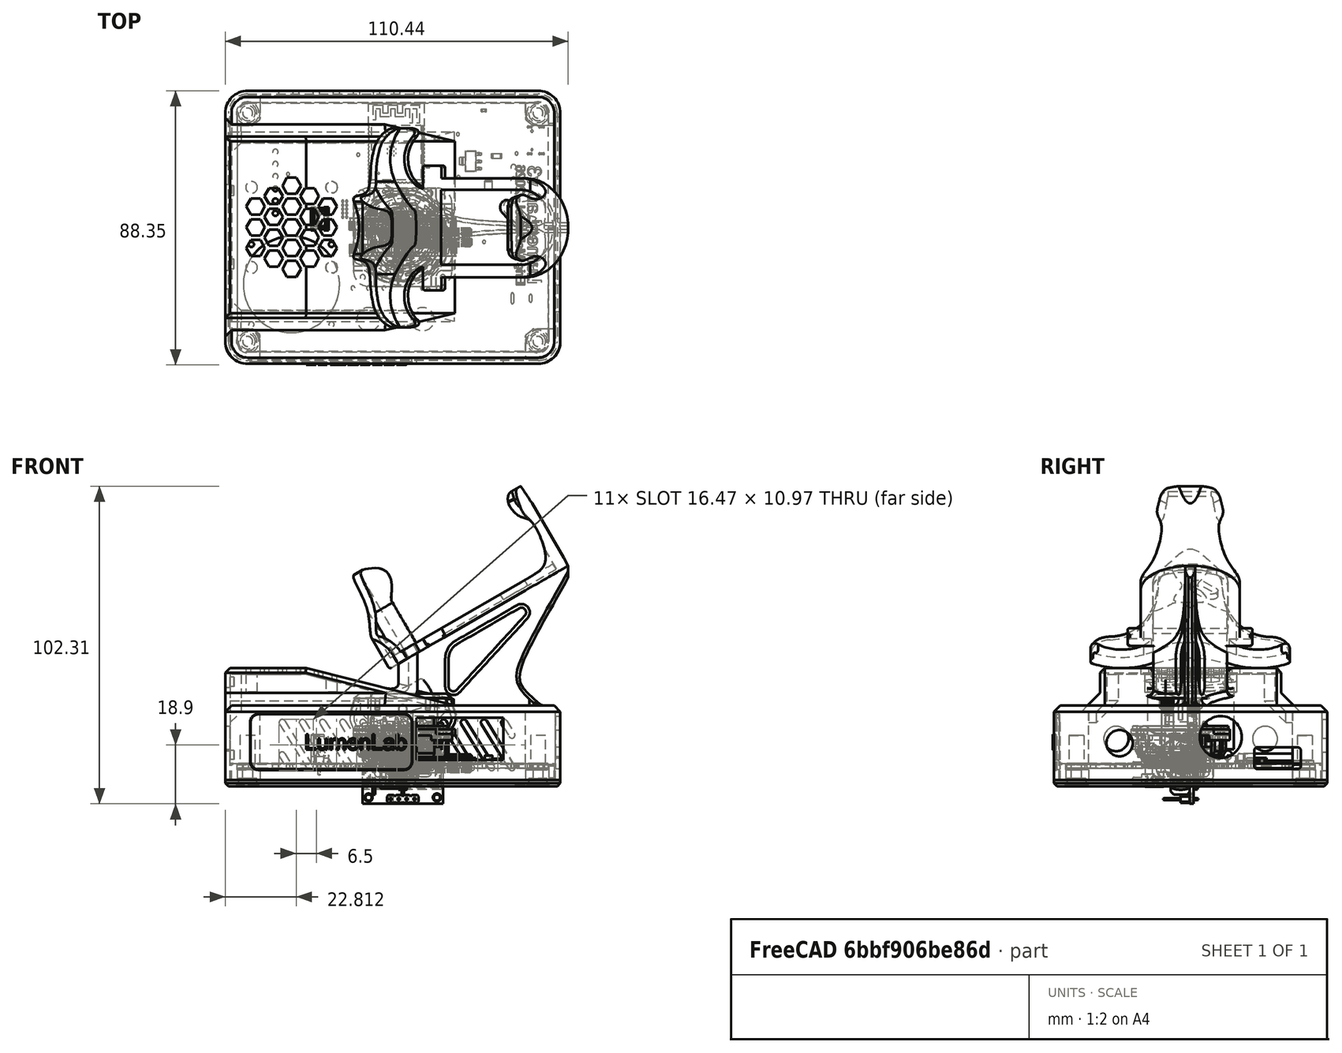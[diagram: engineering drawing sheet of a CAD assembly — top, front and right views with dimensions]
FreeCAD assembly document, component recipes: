
FREECAD ASSEMBLY — COMPONENT RECIPES ("lumenlab-platform-enclosure")

This assembly document has 22 components, labeled P0..P21 below (a component is one placed body or linked part). 21 of them carry a construction recipe — the FreeCAD feature program that regenerates the part from scratch, quoted from this document or its linked companion documents; the rest are supplied as boundary geometry only. No exploded tour is included for this assembly.
NOTE — document 2 of 2 of this assembly tour. The two overview renders and the header above are repeated from document 1; the component sections below continue where the previous document stopped.
COMPONENT P17 — recipe-attached ("saddle", modeled in this document).
Construction recipe (the document's own serialized feature program — sketch geometry with constraints, then the solid features built on it; lengths are millimeters unless a unit is written):

FEATURE [PartDesign::SubShapeBinder] Binder006
  BindCopyOnChange = 0
  BindMode = 0
  ClaimChildren = false
  Context = -> Body016 [Binder006.]
  Fuse = false
  MakeFace = true
  OffsetFill = false
  OffsetIntersection = false
  OffsetJoinType = 0
  OffsetOpenResult = false
  PartialLoad = false
  Refine = true
  Relative = true
  Support = -> [Body001]
  _Version = 2
FEATURE [PartDesign::SubShapeBinder] Binder007
  BindCopyOnChange = 0
  BindMode = 0
  ClaimChildren = false
  Context = -> Body016 [Binder007.]
  Fuse = false
  MakeFace = true
  OffsetFill = false
  OffsetIntersection = false
  OffsetJoinType = 0
  OffsetOpenResult = false
  PartialLoad = false
  Refine = true
  Relative = true
  Support = -> [PS3_Controller]
  _Version = 2
FEATURE [Sketcher::SketchObject] Sketch050
  ArcFitTolerance = 1e-06
  AttachmentSupport = -> [Binder007]
  ExternalGeometry = -> [Binder007]
  ExternalTypes = [0,0,0,0,0,0,0]
  FullyConstrained = false
  MakeInternals = false
  MapMode = 5
  Placement = pos=(-15.7431,5e-16,27.2678) rot=(0.965926,0,0.258819;3.14159rad)
  _ExternalGeoVersion = 1
  sketch-geometry (44):
    g0: LineSegment StartX=14.7182 StartY=28.9768 StartZ=0 EndX=18.1182 EndY=28.9768 EndZ=0
    g1: LineSegment StartX=14.7182 StartY=-35.1235 StartZ=0 EndX=18.1182 EndY=-35.1235 EndZ=0
    g2: ArcOfCircle CenterX=28.7277 CenterY=18.953 CenterZ=0 NormalX=0 NormalY=0 NormalZ=1 AngleXU=0 Radius=17.2262 StartAngle=2.52054 EndAngle=3.77326
    g3: ArcOfCircle CenterX=28.7277 CenterY=-25.0997 CenterZ=0 NormalX=0 NormalY=0 NormalZ=1 AngleXU=0 Radius=17.2262 StartAngle=2.50993 EndAngle=3.76265
    g4: ArcOfCircle CenterX=28.7277 CenterY=18.953 CenterZ=0 NormalX=0 NormalY=0 NormalZ=1 AngleXU=0 Radius=10 StartAngle=2.27093 EndAngle=4.40385
    g5: ArcOfCircle CenterX=28.7277 CenterY=-25.0997 CenterZ=0 NormalX=0 NormalY=0 NormalZ=1 AngleXU=0 Radius=10 StartAngle=1.87933 EndAngle=3.98193
    g6: LineSegment StartX=25.6911 StartY=9.42521 StartZ=0 EndX=25.6911 EndY=16.3262 EndZ=0
    g7: LineSegment StartX=25.6911 StartY=-15.5719 StartZ=0 EndX=25.6911 EndY=-22.3413 EndZ=0
    g8: LineSegment StartX=32.5059 StartY=12.8763 StartZ=0 EndX=62.0059 EndY=12.8763 EndZ=0
    g9: ArcOfCircle CenterX=62.0059 CenterY=-3.07369 CenterZ=0 NormalX=0 NormalY=0 NormalZ=1 AngleXU=0 Radius=15.95 StartAngle=4.71239 EndAngle=7.85398
    g10: Circle [constr] CenterX=18.1182 CenterY=28.9768 CenterZ=0 NormalX=0 NormalY=0 NormalZ=1 AngleXU=0 Radius=1
    g11: Circle [constr] CenterX=24.3003 CenterY=29.1669 CenterZ=0 NormalX=0 NormalY=0 NormalZ=1 AngleXU=0 Radius=1
    g12: Circle [constr] CenterX=22.2845 CenterY=26.6006 CenterZ=0 NormalX=0 NormalY=0 NormalZ=1 AngleXU=0 Radius=1
    g13: BSplineCurve PolesCount=3 KnotsCount=2 Degree=2 IsPeriodic=0
    g14: GeomPoint [constr] X=18.1182 Y=28.9768 Z=0
    g15: GeomPoint [constr] X=22.2845 Y=26.6006 Z=0
    g16: Circle [constr] CenterX=18.1182 CenterY=-35.1235 CenterZ=0 NormalX=0 NormalY=0 NormalZ=1 AngleXU=0 Radius=1
    g17: Circle [constr] CenterX=24.3003 CenterY=-35.3594 CenterZ=0 NormalX=0 NormalY=0 NormalZ=1 AngleXU=0 Radius=1
    g18: Circle [constr] CenterX=22.0556 CenterY=-32.5484 CenterZ=0 NormalX=0 NormalY=0 NormalZ=1 AngleXU=0 Radius=1
    g19: BSplineCurve PolesCount=3 KnotsCount=2 Degree=2 IsPeriodic=0
    g20: GeomPoint [constr] X=18.1182 Y=-35.1235 Z=0
    g21: GeomPoint [constr] X=22.0556 Y=-32.5484 Z=0
    g22: Circle [constr] CenterX=14.8254 CenterY=8.78113 CenterZ=0 NormalX=0 NormalY=0 NormalZ=1 AngleXU=0 Radius=1
    g23: Circle [constr] CenterX=22.5059 CenterY=-3.07336 CenterZ=0 NormalX=0 NormalY=0 NormalZ=1 AngleXU=0 Radius=1
    g24: Circle [constr] CenterX=14.8254 CenterY=-14.9279 CenterZ=0 NormalX=0 NormalY=0 NormalZ=1 AngleXU=0 Radius=1
    g25: BSplineCurve PolesCount=3 KnotsCount=2 Degree=2 IsPeriodic=0
    g26: GeomPoint [constr] X=14.8254 Y=8.78113 Z=0
    g27: GeomPoint [constr] X=14.8254 Y=-14.9279 Z=0
    g28: LineSegment [constr] StartX=29.7892 StartY=4.11327 StartZ=0 EndX=22.5059 EndY=-3.07336 EndZ=0
    g29: LineSegment [constr] StartX=29.7892 StartY=-10.26 StartZ=0 EndX=22.5059 EndY=-3.07336 EndZ=0
    g30: LineSegment StartX=32.5059 StartY=12.8763 StartZ=0 EndX=32.5059 EndY=16.3262 EndZ=0
    g31: LineSegment StartX=31.7836 StartY=17.0486 StartZ=0 EndX=26.4134 EndY=17.0486 EndZ=0
    g32: LineSegment StartX=62.0059 StartY=-19.0237 StartZ=0 EndX=32.5059 EndY=-19.0237 EndZ=0
    g33: LineSegment StartX=32.5059 StartY=-19.0237 StartZ=0 EndX=32.5059 EndY=-22.3413 EndZ=0
    g34: LineSegment StartX=31.7836 StartY=-23.0637 StartZ=0 EndX=26.4134 EndY=-23.0637 EndZ=0
    g35: ArcOfCircle CenterX=31.7836 CenterY=16.3262 CenterZ=0 NormalX=0 NormalY=0 NormalZ=1 AngleXU=0 Radius=0.722378 StartAngle=2.3e-15 EndAngle=1.5708
    g36: GeomPoint [constr] X=32.5059 Y=17.0486 Z=0
    g37: ArcOfCircle CenterX=26.4134 CenterY=16.3262 CenterZ=0 NormalX=0 NormalY=0 NormalZ=1 AngleXU=0 Radius=0.722378 StartAngle=1.5708 EndAngle=3.14159
    g38: GeomPoint [constr] X=25.6911 Y=17.0486 Z=0
    g39: ArcOfCircle CenterX=31.7836 CenterY=-22.3413 CenterZ=0 NormalX=0 NormalY=0 NormalZ=1 AngleXU=0 Radius=0.722378 StartAngle=4.71239 EndAngle=6.28319
    g40: GeomPoint [constr] X=32.5059 Y=-23.0637 Z=0
    g41: ArcOfCircle CenterX=26.4134 CenterY=-22.3413 CenterZ=0 NormalX=0 NormalY=0 NormalZ=1 AngleXU=0 Radius=0.722378 StartAngle=3.14159 EndAngle=4.71239
    g42: GeomPoint [constr] X=25.6911 Y=-23.0637 Z=0
    g43: LineSegment [constr] StartX=32.5059 StartY=12.8763 StartZ=0 EndX=32.5059 EndY=-19.0237 EndZ=0
  constraints (91):
    c: Horizontal(g0,g-3)
    c: Horizontal(g1,g-4)
    c: Coincident(g0,g-3)
    c: DistanceX(g0,g0) = 3.4
    c: Coincident(g1,g-4)
    c: DistanceX(g1,g1) = 3.4
    c: Coincident(g2,g-3)
    c: Coincident(g2,g0)
    c: Coincident(g3,g-4)
    c: Coincident(g3,g1)
    c: Coincident(g4,g2)
    c: Coincident(g5,g3)
    c: Radius(g4) = 10
    c: Radius(g5) = 10
    c: Vertical(g4,g5)
    c: Coincident(g6,g4)
    c: Vertical(g6)
    c: Coincident(g7,g5)
    c: Vertical(g7)
    c: Horizontal(g8)
    c: Tangent(g8,g9) = 1.5708
    c: Weight(g10) = 1
    c: Equal(g10,g11)
    c: Equal(g10,g12)
    c: InternalAlignment(g10,g13)
    c: InternalAlignment(g11,g13)
    c: InternalAlignment(g12,g13)
    c: InternalAlignment(g14,g13)
    c: InternalAlignment(g15,g13)
    c: Coincident(g10,g0)
    c: Coincident(g12,g4)
    c: Weight(g16) = 1
    c: Equal(g16,g17)
    c: Equal(g16,g18)
    c: InternalAlignment(g16,g19)
    c: InternalAlignment(g17,g19)
    c: InternalAlignment(g18,g19)
    c: InternalAlignment(g20,g19)
    c: InternalAlignment(g21,g19)
    c: Coincident(g16,g1)
    c: Coincident(g18,g5)
    c: Vertical(g11,g17)
    c: Weight(g22) = 1
    c: Equal(g22,g23)
    c: Equal(g22,g24)
    c: InternalAlignment(g22,g25)
    c: InternalAlignment(g23,g25)
    c: InternalAlignment(g24,g25)
    c: InternalAlignment(g26,g25)
    c: InternalAlignment(g27,g25)
    c: Vertical(g25,g25)
    c: Coincident(g28,g-8)
    c: Coincident(g28,g23)
    c: Coincident(g29,g-8)
    c: Coincident(g29,g23)
    c: Equal(g28,g29)
    c: Coincident(g25,g2)
    c: Coincident(g25,g3)
    c: DistanceX(g8,g8) = 29.5
    c: Coincident(g30,g8)
    c: Vertical(g30)
    c: Horizontal(g31)
    c: Horizontal(g32)
    c: Coincident(g33,g32)
    c: Vertical(g33)
    c: Horizontal(g34)
    c: PointOnObject(g36,g30)
    c: PointOnObject(g36,g31)
    c: Tangent(g30,g35) = -1.5708
    c: Tangent(g31,g35) = -1.5708
    c: PointOnObject(g38,g6)
    c: PointOnObject(g38,g31)
    c: Tangent(g6,g37) = 1.5708
    c: Tangent(g31,g37) = -1.5708
    c: PointOnObject(g40,g33)
    c: PointOnObject(g40,g34)
    c: Tangent(g33,g39) = 1.5708
    c: Tangent(g34,g39) = 1.5708
    c: PointOnObject(g42,g7)
    c: PointOnObject(g42,g34)
    c: Tangent(g7,g41) = -1.5708
    c: Tangent(g34,g41) = 1.5708
    c: Equal(g35,g37)
    c: Equal(g35,g39)
    c: Equal(g35,g41)
    c: DistanceX(g23,g9) = 39.5
    c: Tangent(g32,g9) = 1.5708
    c: Distance(g32,g8) = 31.9
    c: Coincident(g43,g8)
    c: Coincident(g43,g32)
    c: Vertical(g43)
FEATURE [PartDesign::Pad] Pad023
  Direction = (0.5,0,-0.866025)
  Length = 3
  Length2 = 10
  Profile = -> Sketch050
  ReferenceAxis = -> Sketch050 [N_Axis]
  Refine = true
  SideType = 0
  Suppressed = false
  Type = 0
  Type2 = 0
FEATURE [Sketcher::SketchObject] Sketch051
  ArcFitTolerance = 1e-06
  AttachmentSupport = -> [Pad023]
  ExternalGeometry = -> [Binder007,Pad023]
  ExternalTypes = [0,0,0,0,0,0,0,0]
  FullyConstrained = false
  MakeInternals = false
  MapMode = 5
  Placement = pos=(-15.7431,0,27.2678) rot=(0,-1,0;0.523599rad)
  _ExternalGeoVersion = 1
  sketch-geometry (24):
    g0: ArcOfCircle CenterX=28.7277 CenterY=25.0997 CenterZ=0 NormalX=0 NormalY=0 NormalZ=1 AngleXU=0 Radius=15.1872 StartAngle=2.42075 EndAngle=3.62843
    g1: LineSegment [constr] StartX=15.3049 StartY=17.9946 StartZ=0 EndX=15.3049 EndY=-11.8479 EndZ=0
    g2: LineSegment StartX=17.3182 StartY=35.1235 StartZ=0 EndX=14.7182 EndY=35.1235 EndZ=0
    g3-g9: Circle [constr] x7 (B-spline internal-alignment scaffolding for g10; pole/knot coordinates omitted)
    g10: BSplineCurve PolesCount=7 KnotsCount=5 Degree=3 IsPeriodic=0
    g11-g15: GeomPoint [constr] x5 (B-spline internal-alignment scaffolding for g10; pole/knot coordinates omitted)
    g16: LineSegment [constr] StartX=21.176 StartY=8.55829 StartZ=0 EndX=21.176 EndY=-2.41156 EndZ=0
    g17: LineSegment [constr] StartX=23.1344 StartY=12.0134 StartZ=0 EndX=23.1344 EndY=-10.8872 EndZ=0
    g18: ArcOfCircle CenterX=28.7277 CenterY=-18.953 CenterZ=0 NormalX=0 NormalY=0 NormalZ=1 AngleXU=0 Radius=15.1872 StartAngle=2.65476 EndAngle=3.86243
    g19: LineSegment StartX=14.7182 StartY=-28.9768 StartZ=0 EndX=17.3182 EndY=-28.9768 EndZ=0
    g20: LineSegment [constr] StartX=23.1344 StartY=10.26 StartZ=0 EndX=29.7892 EndY=10.26 EndZ=0
    g21: LineSegment [constr] StartX=23.1344 StartY=-4.11327 StartZ=0 EndX=29.7892 EndY=-4.11327 EndZ=0
    g22: LineSegment [constr] StartX=21.176 StartY=8.55829 StartZ=0 EndX=29.7892 EndY=10.26 EndZ=0
    g23: LineSegment [constr] StartX=21.176 StartY=-2.41156 StartZ=0 EndX=29.7892 EndY=-4.11327 EndZ=0
  constraints (42):
    c: Distance(g-3) = 69.7881
    c: Distance(g-3) = 69.7881
    c: PointOnObject(g0,g-6)
    c: DistanceX(g0,g-6) = 0.8
    c: Vertical(g1)
    c: Coincident(g2,g0)
    c: Coincident(g2,g-6)
    c: Coincident(g0,g1)
    c: Weight(g3) = 1
    c: Equal(g3,g4)
    c: Equal(g3,g5)
    c: Equal(g3,g6)
    c: Equal(g3,g8)
    c: Equal(g3,g9)
    c: InternalAlignment(g3-g9 -> g10) x7
    c: InternalAlignment(g11-g15 -> g10) x5
    c: Coincident(g9,g1)
    c: Coincident(g10,g0)
    c: Coincident(g16,g4)
    c: Vertical(g16)
    c: Coincident(g16,g8)
    c: PointOnObject(g5,g17)
    c: PointOnObject(g6,g17)
    c: Coincident(g18,g-19)
    c: Coincident(g18,g10)
    c: Horizontal(g-17,g18)
    c: DistanceX(g18,g-17) = 0.8
    c: Vertical(g17)
    c: Coincident(g19,g-19)
    c: Coincident(g19,g18)
    c: Coincident(g20,g5)
    c: Coincident(g20,g-4)
    c: Horizontal(g20)
    c: Coincident(g21,g7)
    c: Coincident(g21,g-4)
    c: Symmetric(g7,g5,g6)
    c: Coincident(g22,g4)
    c: Coincident(g22,g20)
    c: Coincident(g23,g8)
    c: Coincident(g23,g21)
    c: Equal(g23,g22)
    c: Symmetric(g7,g5,g13)
FEATURE [Sketcher::SketchObject] Sketch054
  ArcFitTolerance = 1e-06
  AttachmentOffset = pos=(0,0,5) rot=(0,0,1;0rad)
  ExternalTypes = [0,0,0]
  FullyConstrained = false
  MakeInternals = false
  MapMode = 5
  Placement = pos=(30.1283,5e-14,17.3946) rot=(0.447214,0.447214,0.774597;1.82348rad)
  _ExternalGeoVersion = 1
  sketch-geometry (24):
    g0: BSplineCurve PolesCount=4 KnotsCount=2 Degree=3 IsPeriodic=0
    g1: ArcOfCircle CenterX=-21.3632 CenterY=31.5542 CenterZ=0 NormalX=0 NormalY=0 NormalZ=1 AngleXU=0 Radius=7.61389 StartAngle=1.74061 EndAngle=3.15052
    g2: LineSegment [constr] StartX=-5.38635 StartY=60.4862 StartZ=0 EndX=-5.38635 EndY=32.2414 EndZ=0
    g3: LineSegment [constr] StartX=-5.38635 StartY=32.2414 StartZ=0 EndX=3.07336 EndY=32.2414 EndZ=0
    g4: LineSegment [constr] StartX=3.07336 StartY=32.2414 StartZ=0 EndX=3.07336 EndY=60.4862 EndZ=0
    g5: LineSegment [constr] StartX=3.07336 StartY=60.4862 StartZ=0 EndX=-5.38635 EndY=60.4862 EndZ=0
    g6: LineSegment [constr] StartX=11.5331 StartY=60.4862 StartZ=0 EndX=3.07336 EndY=60.4862 EndZ=0
    g7: LineSegment [constr] StartX=3.07336 StartY=60.4862 StartZ=0 EndX=3.07336 EndY=32.2414 EndZ=0
    g8: LineSegment [constr] StartX=3.07336 StartY=32.2414 StartZ=0 EndX=11.5331 EndY=32.2414 EndZ=0
    g9: LineSegment [constr] StartX=11.5331 StartY=32.2414 StartZ=0 EndX=11.5331 EndY=60.4862 EndZ=0
    g10: LineSegment [constr] StartX=11.5331 StartY=60.4862 StartZ=0 EndX=-5.38635 EndY=32.2414 EndZ=0
    g11: LineSegment [constr] StartX=-5.38635 StartY=60.4862 StartZ=0 EndX=11.5331 EndY=32.2414 EndZ=0
    g12: GeomPoint [constr] X=3.07336 Y=46.3638 Z=0
    g13: LineSegment [constr] StartX=-28.9768 StartY=60.4862 StartZ=0 EndX=-5.38635 EndY=60.4862 EndZ=0
    g14: LineSegment [constr] StartX=11.5331 StartY=60.4862 StartZ=0 EndX=35.1235 EndY=60.4862 EndZ=0
    g15: ArcOfCircle CenterX=27.5795 CenterY=31.4875 CenterZ=0 NormalX=0 NormalY=0 NormalZ=1 AngleXU=0 Radius=7.54399 StartAngle=6.283 EndAngle=7.68194
    g16: BSplineCurve PolesCount=4 KnotsCount=2 Degree=3 IsPeriodic=0
    g17: LineSegment StartX=-28.9768 StartY=31.4862 StartZ=0 EndX=-28.9768 EndY=31.4861 EndZ=0
    g18: LineSegment StartX=-28.9768 StartY=31.4861 StartZ=0 EndX=-33.2243 EndY=31.4861 EndZ=0
    g19: LineSegment StartX=-33.2243 StartY=31.4861 StartZ=0 EndX=-33.2243 EndY=61.0561 EndZ=0
    g20: LineSegment StartX=39.371 StartY=31.4861 StartZ=0 EndX=39.371 EndY=61.0561 EndZ=0
    g21: LineSegment StartX=35.1235 StartY=31.4861 StartZ=0 EndX=39.371 EndY=31.4861 EndZ=0
    g22: LineSegment StartX=-5.38635 StartY=60.4862 StartZ=0 EndX=11.5331 EndY=60.4862 EndZ=0
    g23: LineSegment StartX=-33.2243 StartY=61.0561 StartZ=0 EndX=39.371 EndY=61.0561 EndZ=0
  constraints (47):
    c: Coincident(g1,g-3) = -1.5708
    c: Tangent(g0,g1) = -1.5708
    c: Coincident(g2,g3)
    c: Coincident(g3,g4)
    c: Coincident(g4,g5)
    c: Coincident(g5,g2)
    c: Vertical(g2)
    c: Vertical(g4)
    c: Horizontal(g3)
    c: Horizontal(g5)
    c: Coincident(g2,g0)
    c: Coincident(g6,g7)
    c: Coincident(g7,g8)
    c: Coincident(g8,g9)
    c: Coincident(g9,g6)
    c: Horizontal(g6)
    c: Horizontal(g8)
    c: Vertical(g7)
    c: Vertical(g9)
    c: Coincident(g7,g3)
    c: Coincident(g10,g6)
    c: Coincident(g10,g2)
    c: Coincident(g11,g2)
    c: Coincident(g11,g8)
    c: Symmetric(g10,g10,g12)
    c: PointOnObject(g12,g4)
    c: Coincident(g13,g-3)
    c: Coincident(g13,g2)
    c: Horizontal(g13)
    c: Coincident(g14,g6)
    c: Coincident(g14,g-4)
    c: Equal(g14,g13)
    c: Tangent(g16,g15) = 1.5708
    c: Tangent(g1,g17) = -1.5708
    c: Coincident(g17,g18)
    c: Coincident(g18,g19)
    c: Vertical(g19)
    c: Horizontal(g18)
    c: DistanceY(g19,g19) = 29.57
    c: Symmetric(g16,g22,g4)
    c: Symmetric(g18,g21,g4)
    c: Symmetric(g18,g21,g4)
    c: Symmetric(g19,g20,g4)
    c: Symmetric(g19,g20,g4)
    c: Coincident(g23,g19)
    c: Coincident(g23,g20)
    c: Coincident(g21,g15)
FEATURE [PartDesign::Plane] DatumPlane003
  AttachmentOffset = pos=(0,0,-1) rot=(0,0,1;0rad)
  AttachmentSupport = -> [Binder006]
  Length = 92.4589
  MapMode = 5
  Placement = pos=(0,0,17.6498) rot=(0,0,1;0rad)
  ResizeMode = 0
  Width = 78.2686
FEATURE [PartDesign::Plane] DatumPlane004
  AttachmentOffset = pos=(0,0,-1) rot=(0,0,1;0rad)
  AttachmentSupport = -> [Binder006]
  Length = 120.069
  MapMode = 5
  Placement = pos=(5.15041,3.8e-15,20.5239) rot=(0,1,0;0.24587rad)
  ResizeMode = 0
  Width = 80.411
FEATURE [Sketcher::SketchObject] Sketch060
  ArcFitTolerance = 1e-06
  AttachmentSupport = -> [DatumPlane004]
  ExternalTypes = [0]
  FullyConstrained = false
  MakeInternals = false
  MapMode = 5
  Placement = pos=(5.15041,3.8e-15,20.5239) rot=(0,1,0;0.24587rad)
  _ExternalGeoVersion = 1
  sketch-geometry (4):
    g0: LineSegment StartX=-96.5363 StartY=-61.7548 StartZ=0 EndX=96.3187 EndY=-61.7548 EndZ=0
    g1: LineSegment StartX=96.3187 StartY=-61.7548 StartZ=0 EndX=96.3187 EndY=65.0481 EndZ=0
    g2: LineSegment StartX=96.3187 StartY=65.0481 StartZ=0 EndX=-96.5363 EndY=65.0481 EndZ=0
    g3: LineSegment StartX=-96.5363 StartY=65.0481 StartZ=0 EndX=-96.5363 EndY=-61.7548 EndZ=0
  constraints (8):
    c: Coincident(g0,g1)
    c: Coincident(g1,g2)
    c: Coincident(g2,g3)
    c: Coincident(g3,g0)
    c: Horizontal(g0)
    c: Horizontal(g2)
    c: Vertical(g1)
    c: Vertical(g3)
FEATURE [Sketcher::SketchObject] Sketch063
  ArcFitTolerance = 1e-06
  AttachmentOffset = pos=(0,0,15) rot=(0,0,1;0rad)
  AttachmentSupport = -> [Pad023]
  ExternalGeometry = -> [Binder007,Pad023]
  ExternalTypes = [0,0,0,0,0,0,0,0]
  FullyConstrained = false
  MakeInternals = false
  MapMode = 5
  Placement = pos=(-23.2431,0,40.2582) rot=(0,-1,0;0.523599rad)
  _ExternalGeoVersion = 1
  sketch-geometry (24):
    g0: ArcOfCircle CenterX=28.7277 CenterY=25.0997 CenterZ=0 NormalX=0 NormalY=0 NormalZ=1 AngleXU=0 Radius=15.1872 StartAngle=2.42075 EndAngle=3.62843
    g1: LineSegment [constr] StartX=15.3049 StartY=17.9946 StartZ=0 EndX=15.3049 EndY=-11.8479 EndZ=0
    g2: LineSegment StartX=17.3182 StartY=35.1235 StartZ=0 EndX=14.7182 EndY=35.1235 EndZ=0
    g3-g9: Circle [constr] x7 (B-spline internal-alignment scaffolding for g10; pole/knot coordinates omitted)
    g10: BSplineCurve PolesCount=7 KnotsCount=5 Degree=3 IsPeriodic=0
    g11-g15: GeomPoint [constr] x5 (B-spline internal-alignment scaffolding for g10; pole/knot coordinates omitted)
    g16: LineSegment [constr] StartX=21.1816 StartY=8.52334 StartZ=0 EndX=21.1816 EndY=-2.32745 EndZ=0
    g17: LineSegment [constr] StartX=23.029 StartY=12.0134 StartZ=0 EndX=23.029 EndY=-10.8872 EndZ=0
    g18: ArcOfCircle CenterX=28.7277 CenterY=-18.953 CenterZ=0 NormalX=0 NormalY=0 NormalZ=1 AngleXU=0 Radius=15.1872 StartAngle=2.65476 EndAngle=3.86243
    g19: LineSegment StartX=14.7182 StartY=-28.9768 StartZ=0 EndX=17.3182 EndY=-28.9768 EndZ=0
    g20: LineSegment [constr] StartX=23.029 StartY=10.26 StartZ=0 EndX=29.7892 EndY=10.26 EndZ=0
    g21: LineSegment [constr] StartX=23.029 StartY=-4.11329 StartZ=0 EndX=29.7892 EndY=-4.11327 EndZ=0
    g22: LineSegment [constr] StartX=21.1816 StartY=8.52334 StartZ=0 EndX=29.7892 EndY=10.26 EndZ=0
    g23: LineSegment [constr] StartX=21.1917 StartY=-2.32745 StartZ=0 EndX=29.7892 EndY=-4.11327 EndZ=0
  constraints (40):
    c: Distance(g-3) = 69.7881
    c: Distance(g-3) = 69.7881
    c: PointOnObject(g0,g-6)
    c: DistanceX(g0,g-6) = 0.8
    c: Vertical(g1)
    c: Coincident(g2,g0)
    c: Coincident(g2,g-6)
    c: Coincident(g0,g1)
    c: Weight(g3) = 1
    c: Equal(g3,g4)
    c: Equal(g3,g5)
    c: Equal(g3,g6)
    c: Equal(g3,g8)
    c: Equal(g3,g9)
    c: InternalAlignment(g3-g9 -> g10) x7
    c: InternalAlignment(g11-g15 -> g10) x5
    c: Coincident(g9,g1)
    c: Coincident(g10,g0)
    c: Coincident(g16,g4)
    c: Vertical(g16)
    c: Coincident(g16,g8)
    c: PointOnObject(g5,g17)
    c: PointOnObject(g6,g17)
    c: Coincident(g18,g-19)
    c: Coincident(g18,g10)
    c: Horizontal(g-17,g18)
    c: DistanceX(g18,g-17) = 0.8
    c: Coincident(g19,g-19)
    c: Coincident(g19,g18)
    c: Coincident(g20,g5)
    c: Coincident(g20,g-4)
    c: Horizontal(g20)
    c: Coincident(g21,g7)
    c: Coincident(g21,g-4)
    c: Equal(g21,g20)
    c: Symmetric(g7,g5,g6)
    c: Symmetric(g7,g5,g13)
    c: Coincident(g22,g4)
    c: Coincident(g22,g20)
    c: Equal(g22,g23)
FEATURE [Sketcher::SketchObject] Sketch064
  ArcFitTolerance = 1e-06
  AttachmentOffset = pos=(0,0,29) rot=(0,0,1;0rad)
  AttachmentSupport = -> [Pad023]
  ExternalGeometry = -> [Binder007,Pad023]
  ExternalTypes = [0,0,0,0,0,0,0,0]
  FullyConstrained = false
  MakeInternals = false
  MapMode = 5
  Placement = pos=(-30.2431,0,52.3826) rot=(0,-1,0;0.523599rad)
  _ExternalGeoVersion = 1
  sketch-geometry (22):
    g0: ArcOfCircle CenterX=28.7277 CenterY=25.0997 CenterZ=0 NormalX=0 NormalY=0 NormalZ=1 AngleXU=0 Radius=15.1872 StartAngle=2.42075 EndAngle=3.62843
    g1: LineSegment [constr] StartX=15.3049 StartY=17.9946 StartZ=0 EndX=15.3049 EndY=-11.8479 EndZ=0
    g2: LineSegment StartX=17.3182 StartY=35.1235 StartZ=0 EndX=14.7182 EndY=35.1235 EndZ=0
    g3-g9: Circle [constr] x7 (B-spline internal-alignment scaffolding for g10; pole/knot coordinates omitted)
    g10: BSplineCurve PolesCount=7 KnotsCount=5 Degree=3 IsPeriodic=0
    g11-g15: GeomPoint [constr] x5 (B-spline internal-alignment scaffolding for g10; pole/knot coordinates omitted)
    g16: LineSegment [constr] StartX=20.0417 StartY=8.54077 StartZ=0 EndX=20.0417 EndY=-2.37827 EndZ=0
    g17: LineSegment [constr] StartX=30.4048 StartY=12.0134 StartZ=0 EndX=30.4048 EndY=-10.8872 EndZ=0
    g18: ArcOfCircle CenterX=28.7277 CenterY=-18.953 CenterZ=0 NormalX=0 NormalY=0 NormalZ=1 AngleXU=0 Radius=15.1872 StartAngle=2.65476 EndAngle=3.86243
    g19: LineSegment StartX=14.7182 StartY=-28.9768 StartZ=0 EndX=17.3182 EndY=-28.9768 EndZ=0
    g20: LineSegment [constr] StartX=30.4048 StartY=10.26 StartZ=0 EndX=29.7892 EndY=10.26 EndZ=0
    g21: LineSegment [constr] StartX=30.4048 StartY=-4.11327 StartZ=0 EndX=29.7892 EndY=-4.11327 EndZ=0
  constraints (37):
    c: Distance(g-3) = 69.7881
    c: Distance(g-3) = 69.7881
    c: PointOnObject(g0,g-6)
    c: DistanceX(g0,g-6) = 0.8
    c: Vertical(g1)
    c: Coincident(g2,g0)
    c: Coincident(g2,g-6)
    c: Coincident(g0,g1)
    c: Weight(g3) = 1
    c: Equal(g3,g4)
    c: Equal(g3,g5)
    c: Equal(g3,g6)
    c: Equal(g3,g8)
    c: Equal(g3,g9)
    c: InternalAlignment(g3-g9 -> g10) x7
    c: InternalAlignment(g11-g15 -> g10) x5
    c: Coincident(g9,g1)
    c: Coincident(g10,g0)
    c: Coincident(g16,g4)
    c: Vertical(g16)
    c: Coincident(g16,g8)
    c: PointOnObject(g5,g17)
    c: PointOnObject(g6,g17)
    c: PointOnObject(g7,g17)
    c: Coincident(g18,g-19)
    c: Coincident(g18,g10)
    c: Horizontal(g-17,g18)
    c: DistanceX(g18,g-17) = 0.8
    c: Vertical(g17)
    c: Coincident(g19,g-19)
    c: Coincident(g19,g18)
    c: Coincident(g20,g5)
    c: Coincident(g20,g-4)
    c: Horizontal(g20)
    c: Coincident(g21,g7)
    c: Coincident(g21,g-4)
    c: Equal(g21,g20)
FEATURE [PartDesign::AdditiveLoft] AdditiveLoft
  BaseFeature = -> Pad023
  Closed = false
  Profile = -> Sketch051
  Refine = true
  Ruled = true
  Sections = -> [Sketch063,Sketch064]
  Suppressed = false
FEATURE [PartDesign::Pocket] Pocket026
  BaseFeature = -> AdditiveLoft
  Direction = (-0.866025,-1.3e-15,-0.5)
  Length = 50
  Length2 = 5
  Profile = -> Sketch054
  ReferenceAxis = -> Sketch054 [N_Axis]
  Refine = true
  SideType = 0
  Suppressed = false
  Type = 0
  Type2 = 0
FEATURE [Sketcher::SketchObject] Sketch055
  ArcFitTolerance = 1e-06
  AttachmentSupport = -> [Pad023]
  ExternalGeometry = -> [Binder007,Pocket026]
  ExternalTypes = [0,0,0,0]
  FullyConstrained = false
  MakeInternals = false
  MapMode = 5
  Placement = pos=(-15.7431,0,27.2678) rot=(0,-1,0;0.523599rad)
  _ExternalGeoVersion = 1
  sketch-geometry (2):
    g0: ArcOfCircle CenterX=62.0059 CenterY=3.07369 CenterZ=0 NormalX=0 NormalY=0 NormalZ=1 AngleXU=0 Radius=15.95 StartAngle=4.87526 EndAngle=7.69111
    g1: LineSegment StartX=64.5923 StartY=18.8126 StartZ=0 EndX=64.5923 EndY=-12.6652 EndZ=0
  constraints (5):
    c: Coincident(g0,g-5)
    c: PointOnObject(g0,g-6)
    c: PointOnObject(g0,g-6)
    c: Coincident(g1,g0)
    c: Coincident(g1,g0)
FEATURE [PartDesign::Pad] Pad026
  BaseFeature = -> Pocket026
  Direction = (-0.5,0,0.866025)
  Length = 28.2
  Length2 = 10
  Profile = -> Sketch055
  ReferenceAxis = -> Sketch055 [N_Axis]
  Refine = true
  SideType = 0
  Suppressed = false
  Type = 0
  Type2 = 0
FEATURE [Sketcher::SketchObject] Sketch056
  ArcFitTolerance = 1e-06
  AttachmentSupport = -> [Pad026]
  ExternalGeometry = -> [Pad026]
  ExternalTypes = [0,0]
  FullyConstrained = false
  MakeInternals = false
  MapMode = 5
  Placement = pos=(0,-12.8763,0) rot=(1,0,0;1.5708rad)
  _ExternalGeoVersion = 1
  sketch-geometry (21):
    g0: LineSegment StartX=36.7889 StartY=90.1597 StartZ=0 EndX=25.1906 EndY=83.6418 EndZ=0
    g1: LineSegment StartX=25.1906 StartY=83.6418 StartZ=0 EndX=40.1955 EndY=59.564 EndZ=0
    g2: LineSegment StartX=39.277 StartY=91.6181 StartZ=0 EndX=37.2357 EndY=90.4177 EndZ=0
    g3-g9: Circle [constr] x7 (B-spline internal-alignment scaffolding for g10; pole/knot coordinates omitted)
    g10: BSplineCurve PolesCount=7 KnotsCount=5 Degree=3 IsPeriodic=0
    g11-g15: GeomPoint [constr] x5 (B-spline internal-alignment scaffolding for g10; pole/knot coordinates omitted)
    g16: LineSegment [constr] StartX=37.9556 StartY=58.2708 StartZ=0 EndX=41.0861 EndY=60.0782 EndZ=0
    g17: LineSegment StartX=40.1955 StartY=59.564 StartZ=0 EndX=41.0861 EndY=60.0782 EndZ=0
    g18: LineSegment [constr] StartX=37.6687 StartY=90.6677 StartZ=0 EndX=37.2357 EndY=90.4177 EndZ=0
    g19: LineSegment StartX=41.9869 StartY=83.259 StartZ=0 EndX=39.277 EndY=91.6181 EndZ=0
    g20: LineSegment StartX=41.9869 StartY=83.259 StartZ=0 EndX=37.2357 EndY=90.4177 EndZ=0
  constraints (20):
    c: PointOnObject(g0,g-3)
    c: Coincident(g0,g1)
    c: Weight(g3) = 1
    c: Equal(g3, g4-g9) x6
    c: InternalAlignment(g3-g9 -> g10) x7
    c: InternalAlignment(g11-g15 -> g10) x5
    c: Coincident(g9,g0)
    c: Coincident(g-4,g1)
    c: Coincident(g16,g-4)
    c: Coincident(g16,g10)
    c: PointOnObject(g1,g16)
    c: Coincident(g17,g1)
    c: Coincident(g17,g16)
    c: Coincident(g18,g-3)
    c: Parallel(g-3,g18)
    c: Distance(g18,g18) = 0.5
    c: Coincident(g2,g18)
    c: Coincident(g19,g2)
    c: Coincident(g20,g19)
    c: Coincident(g20,g2)
FEATURE [PartDesign::Pocket] Pocket027
  BaseFeature = -> Pad026
  Direction = (0,1,-2e-16)
  Length = 5
  Length2 = 5
  Profile = -> Sketch056
  ReferenceAxis = -> Sketch056 [N_Axis]
  Refine = true
  SideType = 0
  Suppressed = false
  Type = 1
  Type2 = 0
FEATURE [Sketcher::SketchObject] Sketch057
  ArcFitTolerance = 1e-06
  AttachmentOffset = pos=(24,0,81) rot=(0,1,0;1.0472rad)
  AttachmentSupport = -> [XY_Plane076]
  ExternalGeometry = -> [Pocket027]
  ExternalTypes = [0,0,0]
  FullyConstrained = false
  MakeInternals = false
  MapMode = 5
  Placement = pos=(24,0,81) rot=(0,1,0;1.0472rad)
  _ExternalGeoVersion = 1
  sketch-geometry (14):
    g0: LineSegment StartX=-0.200427 StartY=9.95203 StartZ=0 EndX=-0.207796 EndY=-3.95812 EndZ=0
    g1: GeomPoint [constr] X=0 Y=10.6894 Z=0
    g2: GeomPoint [constr] X=0 Y=-4.74102 Z=0
    g3: LineSegment StartX=26.6619 StartY=18.427 StartZ=0 EndX=2.41845 EndY=12.7063 EndZ=0
    g4: LineSegment StartX=26.6619 StartY=-12.2797 StartZ=0 EndX=2.66362 EndY=-6.68203 EndZ=0
    g5: LineSegment StartX=26.6619 StartY=18.427 StartZ=0 EndX=26.6619 EndY=19.0237 EndZ=0
    g6: LineSegment StartX=26.6619 StartY=19.0237 StartZ=0 EndX=-27.4268 EndY=19.0237 EndZ=0
    g7: LineSegment StartX=-27.4268 StartY=19.0237 StartZ=0 EndX=-27.4268 EndY=-12.8763 EndZ=0
    g8: LineSegment StartX=-27.4268 StartY=-12.8763 StartZ=0 EndX=26.6619 EndY=-12.8763 EndZ=0
    g9: LineSegment StartX=26.6619 StartY=-12.8763 StartZ=0 EndX=26.6619 EndY=-12.2797 EndZ=0
    g10: LineSegment [constr] StartX=4.11424 StartY=10.1432 StartZ=0 EndX=-27.4268 EndY=19.0237 EndZ=0
    g11: LineSegment [constr] StartX=4.11424 StartY=-3.99583 StartZ=0 EndX=-27.4268 EndY=-12.8763 EndZ=0
    g12: ArcOfEllipse CenterX=4.11424 CenterY=-3.99583 CenterZ=0 NormalX=0 NormalY=0 NormalZ=1 MajorRadius=4.32231 MinorRadius=2.86452 AngleXU=3.12645 StartAngle=0.00968497 EndAngle=1.23856
    g13: ArcOfEllipse CenterX=4.11424 CenterY=10.1432 CenterZ=0 NormalX=0 NormalY=0 NormalZ=1 MajorRadius=4.32231 MinorRadius=2.86452 AngleXU=-3.06211 StartAngle=5.06358 EndAngle=6.2301
  constraints (25):
    c: Coincident(g3,g5)
    c: Coincident(g5,g-4)
    c: Vertical(g5)
    c: Coincident(g5,g6)
    c: Horizontal(g6)
    c: Coincident(g6,g7)
    c: Vertical(g7)
    c: Coincident(g7,g8)
    c: Coincident(g8,g-5)
    c: Horizontal(g8)
    c: Coincident(g8,g9)
    c: Coincident(g9,g4)
    c: Vertical(g9)
    c: Equal(g5,g9)
    c: Vertical(g11,g10)
    c: Coincident(g10,g6)
    c: Coincident(g11,g7)
    c: Equal(g10,g11)
    c: Coincident(g12,g11)
    c: Coincident(g13,g10)
    c: Tangent(g0,g13) = -1.5708
    c: Coincident(g13,g3)
    c: Tangent(g0,g12) = -1.5708
    c: Coincident(g12,g4)
    c: Equal(g13,g12)
FEATURE [PartDesign::Pocket] Pocket028
  BaseFeature = -> Pocket027
  Direction = (-0.866025,0,-0.5)
  Length = 14
  Length2 = 5
  Profile = -> Sketch057
  ReferenceAxis = -> Sketch057 [N_Axis]
  Refine = true
  Reversed = true
  SideType = 0
  Suppressed = false
  Type = 1
  Type2 = 0
FEATURE [Sketcher::SketchObject] Sketch058
  ArcFitTolerance = 1e-06
  AttachmentSupport = -> [DatumPlane003]
  ExternalGeometry = -> [Pocket028]
  ExternalTypes = [0,0,0,0,0,0]
  FullyConstrained = false
  MakeInternals = false
  MapMode = 5
  Placement = pos=(0,0,17.6498) rot=(0,0,1;0rad)
  _ExternalGeoVersion = 1
  sketch-geometry (18):
    g0: LineSegment [constr] StartX=39.4556 StartY=3.07369 StartZ=0 EndX=9.90658 EndY=3.07369 EndZ=0
    g1: ArcOfCircle CenterX=39.4556 CenterY=3.07369 CenterZ=0 NormalX=0 NormalY=0 NormalZ=1 AngleXU=0 Radius=13.8351 StartAngle=6.17032 EndAngle=6.39605
    g2-g5: Circle [constr] x4 (B-spline internal-alignment scaffolding for g6; pole/knot coordinates omitted)
    g6: BSplineCurve PolesCount=4 KnotsCount=2 Degree=3 IsPeriodic=0
    g7: GeomPoint [constr] X=4.71827 Y=-8.78113 Z=0
    g8: GeomPoint [constr] X=53.2027 Y=1.51555 Z=0
    g9: BSplineCurve PolesCount=4 KnotsCount=2 Degree=3 IsPeriodic=0
    g10-g13: Circle [constr] x4 (B-spline internal-alignment scaffolding for g9; pole/knot coordinates omitted)
    g14: GeomPoint [constr] X=4.71827 Y=14.9285 Z=0
    g15: GeomPoint [constr] X=53.2027 Y=4.63182 Z=0
    g16: LineSegment StartX=-1.40393 StartY=-8.78113 StartZ=0 EndX=4.71827 EndY=-8.78113 EndZ=0
    g17: LineSegment StartX=4.71827 StartY=14.9285 StartZ=0 EndX=-1.40393 EndY=14.9279 EndZ=0
  constraints (27):
    c: Coincident(g0,g-3)
    c: Horizontal(g0)
    c: Coincident(g1,g0)
    c: PointOnObject(g1,g-3)
    c: PointOnObject(g1,g-3)
    c: Weight(g2) = 1
    c: Equal(g2,g3)
    c: Equal(g2,g4)
    c: Equal(g2,g5)
    c: InternalAlignment(g2-g5 -> g6) x4
    c: InternalAlignment(g7,g6)
    c: InternalAlignment(g8,g6)
    c: Coincident(g5,g1)
    c: InternalAlignment(g10-g15 -> g9) x6
    c: Equal(g2,g10)
    c: Symmetric(g2,g10,g0)
    c: Equal(g3,g11)
    c: Symmetric(g3,g11,g0)
    c: Equal(g4,g12)
    c: Symmetric(g4,g12,g0)
    c: Equal(g5,g13)
    c: Symmetric(g5,g13,g0)
    c: Coincident(g16,g-5)
    c: Horizontal(g16)
    c: Coincident(g6,g16)
    c: Coincident(g17,g9)
    c: Coincident(g17,g-6)
FEATURE [PartDesign::Pad] Pad027
  BaseFeature = -> Pocket028
  Direction = (0,0,1)
  Length = 10
  Length2 = 10
  Profile = -> Sketch058
  ReferenceAxis = -> Sketch058 [N_Axis]
  Refine = true
  SideType = 0
  Suppressed = false
  Type = 2
  Type2 = 0
FEATURE [Sketcher::SketchObject] Sketch059
  ArcFitTolerance = 1e-06
  AttachmentOffset = pos=(0,0,24) rot=(0,0,1;0rad)
  AttachmentSupport = -> [XZ_Plane076]
  ExternalGeometry = -> [Pad027,Binder006]
  ExternalTypes = [0,0]
  FullyConstrained = false
  MakeInternals = false
  MapMode = 5
  Placement = pos=(0,-24,5.3e-15) rot=(1,0,0;1.5708rad)
  _ExternalGeoVersion = 1
  sketch-geometry (20):
    g0: LineSegment [constr] StartX=53.2907 StartY=63.6604 StartZ=0 EndX=53.2907 EndY=-15.1912 EndZ=0
    g1: LineSegment StartX=53.2907 StartY=59.9106 StartZ=0 EndX=53.2907 EndY=11.6114 EndZ=0
    g2-g6: Circle [constr] x5 (B-spline internal-alignment scaffolding for g7; pole/knot coordinates omitted)
    g7: BSplineCurve PolesCount=5 KnotsCount=3 Degree=3 IsPeriodic=0
    g8: GeomPoint [constr] X=53.2907 Y=59.9106 Z=0
    g9: GeomPoint [constr] X=37.6107 Y=27.5538 Z=0
    g10: GeomPoint [constr] X=53.2907 Y=11.6114 Z=0
    g11: LineSegment StartX=17.5054 StartY=38.4181 StartZ=0 EndX=37.4645 EndY=49.9414 EndZ=0
    g12: LineSegment StartX=39.3204 StartY=47.629 StartZ=0 EndX=17.3944 EndY=23.7008 EndZ=0
    g13: LineSegment StartX=14.7885 StartY=24.7142 StartZ=0 EndX=14.7885 EndY=33.7121 EndZ=0
    g14: ArcOfCircle CenterX=16.2885 CenterY=24.7142 CenterZ=0 NormalX=0 NormalY=0 NormalZ=1 AngleXU=0 Radius=1.5 StartAngle=3.14159 EndAngle=5.54142
    g15: GeomPoint [constr] X=14.7885 Y=20.857 Z=0
    g16: ArcOfCircle CenterX=20.2224 CenterY=33.7121 CenterZ=0 NormalX=0 NormalY=0 NormalZ=1 AngleXU=0 Radius=5.43395 StartAngle=2.0944 EndAngle=3.14159
    g17: GeomPoint [constr] X=14.7885 Y=36.8494 Z=0
    g18: ArcOfCircle CenterX=38.2145 CenterY=48.6424 CenterZ=0 NormalX=0 NormalY=0 NormalZ=1 AngleXU=0 Radius=1.5 StartAngle=5.54142 EndAngle=8.37758
    g19: GeomPoint [constr] X=45.9044 Y=54.8142 Z=0
  constraints (28):
    c: Coincident(g0,g-3)
    c: Vertical(g0)
    c: PointOnObject(g1,g0)
    c: Weight(g2) = 1
    c: Equal(g2, g3-g6) x4
    c: InternalAlignment(g2-g6 -> g7) x5
    c: InternalAlignment(g8,g7)
    c: InternalAlignment(g9,g7)
    c: InternalAlignment(g10,g7)
    c: Coincident(g2,g1)
    c: Parallel(g-3,g11)
    c: Vertical(g13)
    c: PointOnObject(g15,g12)
    c: PointOnObject(g15,g13)
    c: Tangent(g12,g14) = 1.5708
    c: Tangent(g13,g14) = 1.5708
    c: PointOnObject(g17,g11)
    c: PointOnObject(g17,g13)
    c: Tangent(g11,g16) = 1.5708
    c: Tangent(g13,g16) = 1.5708
    c: PointOnObject(g19,g11)
    c: PointOnObject(g19,g12)
    c: Tangent(g11,g18) = 1.5708
    c: Tangent(g12,g18) = 1.5708
    c: Coincident(g1,g7)
    c: PointOnObject(g1,g0)
    c: Radius(g14) = 1.5
    c: Equal(g14,g18)
FEATURE [PartDesign::Pocket] Pocket029
  BaseFeature = -> Pad027
  Direction = (0,1,-2e-16)
  Length = 5
  Length2 = 5
  Profile = -> Sketch059
  ReferenceAxis = -> Sketch059 [N_Axis]
  Refine = true
  SideType = 0
  Suppressed = false
  Type = 1
  Type2 = 0
FEATURE [PartDesign::Pocket] Pocket030
  BaseFeature = -> Pocket029
  Direction = (-0.2434,0,-0.969926)
  Length = 5
  Length2 = 5
  Profile = -> Sketch060
  ReferenceAxis = -> Sketch060 [N_Axis]
  Refine = true
  SideType = 0
  Suppressed = false
  Type = 0
  Type2 = 0
FEATURE [PartDesign::Plane] DatumPlane005
  AttachmentOffset = pos=(0,0,0) rot=(1,0,0;1.5708rad)
  AttachmentSupport = -> [Pad023]
  Length = 151.231
  MapMode = 45
  Placement = pos=(10.207,3.00756,40.518) rot=(0.935113,-0.250563,0.250563;1.63783rad)
  ResizeMode = 0
  Width = 164.413
FEATURE [PartDesign::Chamfer] Chamfer012
  Angle = 45
  Base = -> Pocket030 [Edge140,Edge111]
  BaseFeature = -> Pocket030
  ChamferType = 0
  FlipDirection = false
  Refine = true
  Size = 1
  Size2 = 1
  SupportTransform = false
  Suppressed = false
  UseAllEdges = false
FEATURE [PartDesign::Chamfer] Chamfer013
  Angle = 45
  Base = -> Chamfer012 [Edge49,Edge59,Edge52,Edge10,Edge13,Edge9]
  BaseFeature = -> Chamfer012
  ChamferType = 0
  FlipDirection = false
  Refine = true
  Size = 1.2
  Size2 = 1
  SupportTransform = false
  Suppressed = false
  UseAllEdges = false
FEATURE [PartDesign::Fillet] Fillet
  Base = -> Chamfer013 [Edge43,Edge53,Edge52,Edge51,Edge50,Edge46,Edge122,Edge123,Edge124,Edge125,Edge126,Edge127,Edge128,Edge129,Edge130]
  BaseFeature = -> Chamfer013
  Radius = 0.75
  Refine = true
  SupportTransform = false
  Suppressed = false
  UseAllEdges = false
FEATURE [Sketcher::SketchObject] Sketch065
  ArcFitTolerance = 1e-06
  AttachmentSupport = -> [Fillet]
  ExternalGeometry = -> [Fillet]
  ExternalTypes = [0,0]
  FullyConstrained = false
  MakeInternals = false
  MapMode = 5
  Placement = pos=(0,-17.0486,0) rot=(1,0,0;1.5708rad)
  _ExternalGeoVersion = 1
  sketch-geometry (13):
    g0: LineSegment StartX=-0.586007 StartY=52.4207 StartZ=0 EndX=-0.586007 EndY=68.1265 EndZ=0
    g1: LineSegment StartX=-0.586007 StartY=68.1265 StartZ=0 EndX=-12.9047 EndY=69.6005 EndZ=0
    g2: LineSegment StartX=-12.9047 StartY=69.6005 StartZ=0 EndX=-12.9047 EndY=62.3929 EndZ=0
    g3-g7: Circle [constr] x5 (B-spline internal-alignment scaffolding for g8; pole/knot coordinates omitted)
    g8: BSplineCurve PolesCount=5 KnotsCount=3 Degree=3 IsPeriodic=0
    g9: GeomPoint [constr] X=-12.9047 Y=62.3929 Z=0
    g10: GeomPoint [constr] X=-3.53934 Y=56.5917 Z=0
    g11: GeomPoint [constr] X=-3.29935 Y=51.7727 Z=0
    g12: LineSegment StartX=-0.586007 StartY=52.4207 StartZ=0 EndX=-3.29935 EndY=51.7727 EndZ=0
  constraints (15):
    c: Vertical(g0)
    c: Coincident(g1,g0)
    c: Coincident(g2,g1)
    c: Vertical(g2)
    c: Coincident(g2,g-3)
    c: Weight(g3) = 1
    c: Equal(g3, g4-g7) x4
    c: InternalAlignment(g3-g7 -> g8) x5
    c: InternalAlignment(g9,g8)
    c: InternalAlignment(g10,g8)
    c: InternalAlignment(g11,g8)
    c: Coincident(g3,g2)
    c: Coincident(g12,g0)
    c: Coincident(g12,g8)
    c: Coincident(g-4,g8)
FEATURE [PartDesign::Pocket] Pocket031
  BaseFeature = -> Fillet
  Direction = (0,1,-2e-16)
  Length = 5
  Length2 = 5
  Profile = -> Sketch065
  ReferenceAxis = -> Sketch065 [N_Axis]
  Refine = true
  SideType = 0
  Suppressed = false
  Type = 1
  Type2 = 0
FEATURE [PartDesign::Fillet] Fillet001
  Base = -> Pocket031 [Edge227,Edge226]
  BaseFeature = -> Pocket031
  Radius = 2.25
  Refine = true
  SupportTransform = false
  Suppressed = false
  UseAllEdges = false
FEATURE [PartDesign::Plane] DatumPlane006
  AttachmentOffset = pos=(0,0,0) rot=(1,0,0;1.5708rad)
  AttachmentSupport = -> [AdditiveLoft]
  Length = 164.545
  MapMode = 45
  Placement = pos=(-8.12633,3.07336,46.207) rot=(0.375112,0.655473,0.655473;3.85933rad)
  ResizeMode = 0
  Width = 151.738
FEATURE [Sketcher::SketchObject] Sketch066
  ArcFitTolerance = 1e-06
  AttachmentOffset = pos=(0,0,-2) rot=(0,0,1;0rad)
  AttachmentSupport = -> [Fillet001]
  ExternalTypes = [0]
  FullyConstrained = true
  MakeInternals = false
  MapMode = 5
  Placement = pos=(-14.7431,0,25.5358) rot=(0,-1,0;0.523599rad)
  _ExternalGeoVersion = 1
  sketch-geometry (4):
    g0: LineSegment StartX=32.4711 StartY=15.2714 StartZ=0 EndX=61.9711 EndY=15.2714 EndZ=0
    g1: LineSegment StartX=32.4711 StartY=15.2714 StartZ=0 EndX=32.4711 EndY=-8.87855 EndZ=0
    g2: ArcOfCircle CenterX=61.9711 CenterY=3.19645 CenterZ=0 NormalX=0 NormalY=0 NormalZ=1 AngleXU=0 Radius=12.075 StartAngle=4.71239 EndAngle=7.85398
    g3: LineSegment StartX=32.4711 StartY=-8.87855 StartZ=0 EndX=61.9711 EndY=-8.87855 EndZ=0
  constraints (8):
    c: Block(g2)
    c: Coincident(g3,g1)
    c: Coincident(g3,g2)
    c: Horizontal(g3)
    c: Coincident(g0,g2)
    c: Coincident(g0,g1)
    c: Block(g0)
    c: Block(g1)
FEATURE [PartDesign::Pocket] Pocket032
  BaseFeature = -> Fillet001
  Direction = (0.5,0,-0.866025)
  Length = 11.9
  Length2 = 5
  Profile = -> Sketch066
  ReferenceAxis = -> Sketch066 [N_Axis]
  Refine = true
  Reversed = true
  SideType = 0
  Suppressed = false
  Type = 0
  Type2 = 0
FEATURE [PartDesign::Body] Body016  label="saddle"
  AllowCompound = false
  Group = -> [DatumPlane006,DatumPlane005,Binder006,Binder007,Sketch050,Pad023,AdditiveLoft,Sketch051,Sketch063,Sketch064,Sketch054,Pocket026,Sketch055,Pad026,Sketch056,Pocket027,Sketch057,Pocket028,DatumPlane003,DatumPlane004,Sketch058,Pad027,Pocket029,Sketch059,Sketch060,Pocket030,Chamfer012,Chamfer013,Fillet,Sketch065,Pocket031,Fillet001,Sketch066,Pocket032]
  Origin = -> Origin121
  Tip = -> Pocket032
COMPONENT P18 — recipe-attached ("led-clip-saddle", modeled in this document).
Construction recipe (the document's own serialized feature program — sketch geometry with constraints, then the solid features built on it; lengths are millimeters unless a unit is written):

FEATURE [PartDesign::SubShapeBinder] Binder012
  BindCopyOnChange = 0
  BindMode = 0
  ClaimChildren = false
  Context = -> Body017 [Binder012.]
  Fuse = false
  MakeFace = true
  OffsetFill = false
  OffsetIntersection = false
  OffsetJoinType = 0
  OffsetOpenResult = false
  PartialLoad = false
  Refine = true
  Relative = true
  Support = -> [Body016]
  _Version = 2
FEATURE [Sketcher::SketchObject] Sketch061
  ArcFitTolerance = 1e-06
  AttachmentSupport = -> [Binder012]
  ExternalTypes = [0,0,0,0]
  FullyConstrained = false
  MakeInternals = false
  MapMode = 5
  Placement = pos=(-15.7431,0,27.2678) rot=(0,-1,0;0.523599rad)
  _ExternalGeoVersion = 1
  sketch-geometry (4):
    g0: LineSegment StartX=32.4711 StartY=15.2714 StartZ=0 EndX=61.9711 EndY=15.2714 EndZ=0
    g1: LineSegment StartX=32.4711 StartY=15.2714 StartZ=0 EndX=32.4711 EndY=-8.87855 EndZ=0
    g2: LineSegment StartX=32.4711 StartY=-8.87855 StartZ=0 EndX=61.9711 EndY=-8.87855 EndZ=0
    g3: ArcOfCircle CenterX=61.9711 CenterY=3.19645 CenterZ=0 NormalX=0 NormalY=0 NormalZ=1 AngleXU=0 Radius=12.075 StartAngle=4.71239 EndAngle=7.85398
  constraints (11):
    c: Horizontal(g0)
    c: Vertical(g1)
    c: Coincident(g2,g1)
    c: Vertical(g2,g-3)
    c: Distance(g-3,g2) = 4
    c: DistanceY(g1,g1) = 24.15
    c: Vertical(g-3,g1)
    c: Tangent(g3,g2) = -1.5708
    c: Symmetric(g0,g2,g3)
    c: Horizontal(g2)
    c: Coincident(g0,g1)
FEATURE [PartDesign::Pad] Pad028
  Direction = (-0.5,0,0.866025)
  Length = 2
  Length2 = 10
  Profile = -> Sketch061
  ReferenceAxis = -> Sketch061 [N_Axis]
  Refine = true
  Reversed = true
  SideType = 0
  Suppressed = false
  Type = 0
  Type2 = 0
FEATURE [PartDesign::Body] Body017  label="led-clip-saddle"
  AllowCompound = false
  Group = -> [Binder012,Sketch061,Pad028]
  Origin = -> Origin123
  Tip = -> Pad028
COMPONENT P19 — recipe-attached ("led-clip-reflection-saddle", modeled in this document).
Construction recipe (the document's own serialized feature program — sketch geometry with constraints, then the solid features built on it; lengths are millimeters unless a unit is written):

FEATURE [Sketcher::SketchObject] Sketch062
  ArcFitTolerance = 1e-06
  ExternalTypes = [0]
  FullyConstrained = false
  MakeInternals = false
  MapMode = 5
  Placement = pos=(-15.7431,0,27.2678) rot=(0,-1,0;0.523599rad)
  _ExternalGeoVersion = 1
  sketch-geometry (4):
    g0: ArcOfCircle CenterX=61.1508 CenterY=5.68121 CenterZ=0 NormalX=0 NormalY=0 NormalZ=1 AngleXU=0 Radius=2.33897 StartAngle=3.97592 EndAngle=7.11751
    g1: ArcOfCircle CenterX=56.7644 CenterY=9.65805 CenterZ=0 NormalX=0 NormalY=0 NormalZ=1 AngleXU=0 Radius=2.33897 StartAngle=0.834326 EndAngle=3.97592
    g2: LineSegment StartX=59.5798 StartY=3.9484 StartZ=0 EndX=55.1934 EndY=7.92524 EndZ=0
    g3: LineSegment StartX=62.7218 StartY=7.41402 StartZ=0 EndX=58.3355 EndY=11.3909 EndZ=0
  constraints (5):
    c: Tangent(g0,g2) = 1.5708
    c: Tangent(g0,g3) = -1.5708
    c: Tangent(g1,g2) = 1.5708
    c: Tangent(g1,g3) = -1.5708
    c: Equal(g0,g1)
FEATURE [PartDesign::Pad] Pad029
  Direction = (-0.5,0,0.866025)
  Length = 2
  Length2 = 10
  Placement = pos=(-15.7431,0,27.2678) rot=(0,-1,0;0.523599rad)
  Profile = -> Sketch062
  ReferenceAxis = -> Sketch062 [N_Axis]
  Refine = true
  Reversed = true
  SideType = 0
  Suppressed = false
  Type = 0
  Type2 = 0
FEATURE [PartDesign::SubShapeBinder] Binder011
  BindCopyOnChange = 0
  BindMode = 0
  ClaimChildren = false
  Context = -> Body018 [Binder011.]
  Fuse = false
  MakeFace = true
  OffsetFill = false
  OffsetIntersection = false
  OffsetJoinType = 0
  OffsetOpenResult = false
  PartialLoad = false
  Refine = true
  Relative = true
  Support = -> [Body016]
  _Version = 2
FEATURE [PartDesign::Body] Body018  label="led-clip-reflection-saddle"
  AllowCompound = false
  Group = -> [Binder011,Sketch062,Pad029]
  Origin = -> Origin125
  Tip = -> Pad029
COMPONENT P20 — recipe-attached ("saddle-clone", modeled in this document).
Construction recipe (the document's own serialized feature program — sketch geometry with constraints, then the solid features built on it; lengths are millimeters unless a unit is written):

FEATURE [PartDesign::FeatureBase] Clone007
  BaseFeature = -> Body016
  Suppressed = false
FEATURE [PartDesign::Body] Body019  label="saddle-clone"
  AllowCompound = false
  Group = -> [Clone007]
  Origin = -> Origin127
  Tip = -> Clone007
COMPONENT P21 — recipe-attached ("logo-container-top", modeled in this document).
Construction recipe (the document's own serialized feature program — sketch geometry with constraints, then the solid features built on it; lengths are millimeters unless a unit is written):

FEATURE [Sketcher::SketchObject] Sketch068
  ArcFitTolerance = 1e-06
  AttachmentOffset = pos=(0,0,40.25) rot=(0,0,1;0rad)
  AttachmentSupport = -> [Origin129]
  ExternalTypes = [0]
  FullyConstrained = false
  MakeInternals = false
  MapMode = 5
  Placement = pos=(0,-40.25,8.9e-15) rot=(1,0,0;1.5708rad)
  _ExternalGeoVersion = 1
  sketch-geometry (12):
    g0: LineSegment StartX=-48.9928 StartY=13.2908 StartZ=0 EndX=-48.9928 EndY=0.559139 EndZ=0
    g1: LineSegment StartX=-46.4604 StartY=-1.97323 StartZ=0 EndX=0.370511 EndY=-1.97323 EndZ=0
    g2: LineSegment StartX=2.90288 StartY=0.559139 StartZ=0 EndX=2.90288 EndY=13.2908 EndZ=0
    g3: LineSegment StartX=0.370511 StartY=15.8231 StartZ=0 EndX=-46.4604 EndY=15.8231 EndZ=0
    g4: ArcOfCircle CenterX=-46.4604 CenterY=13.2908 CenterZ=0 NormalX=0 NormalY=0 NormalZ=1 AngleXU=0 Radius=2.53236 StartAngle=1.5708 EndAngle=3.14159
    g5: GeomPoint [constr] X=-48.9928 Y=15.8231 Z=0
    g6: ArcOfCircle CenterX=0.370511 CenterY=13.2908 CenterZ=0 NormalX=0 NormalY=0 NormalZ=1 AngleXU=0 Radius=2.53236 StartAngle=1e-16 EndAngle=1.5708
    g7: GeomPoint [constr] X=2.90288 Y=15.8231 Z=0
    g8: ArcOfCircle CenterX=0.370511 CenterY=0.559139 CenterZ=0 NormalX=0 NormalY=0 NormalZ=1 AngleXU=0 Radius=2.53236 StartAngle=4.71239 EndAngle=6.28319
    g9: GeomPoint [constr] X=2.90288 Y=-1.97323 Z=0
    g10: ArcOfCircle CenterX=-46.4604 CenterY=0.559139 CenterZ=0 NormalX=0 NormalY=0 NormalZ=1 AngleXU=0 Radius=2.53236 StartAngle=3.14159 EndAngle=4.71239
    g11: GeomPoint [constr] X=-48.9928 Y=-1.97323 Z=0
  constraints (23):
    c: Vertical(g0)
    c: Vertical(g2)
    c: Horizontal(g1)
    c: Horizontal(g3)
    c: PointOnObject(g5,g0)
    c: PointOnObject(g5,g3)
    c: Tangent(g0,g4) = -1.5708
    c: Tangent(g3,g4) = -1.5708
    c: PointOnObject(g7,g2)
    c: PointOnObject(g7,g3)
    c: Tangent(g2,g6) = -1.5708
    c: Tangent(g3,g6) = -1.5708
    c: PointOnObject(g9,g1)
    c: PointOnObject(g9,g2)
    c: Tangent(g1,g8) = -1.5708
    c: Tangent(g2,g8) = -1.5708
    c: PointOnObject(g11,g0)
    c: PointOnObject(g11,g1)
    c: Tangent(g0,g10) = -1.5708
    c: Tangent(g1,g10) = -1.5708
    c: Equal(g4,g6)
    c: Equal(g4,g8)
    c: Equal(g4,g10)
FEATURE [PartDesign::Pad] Pad030
  Direction = (0,-1,0)
  Length = 1.4
  Length2 = 10
  Profile = -> Sketch068
  ReferenceAxis = -> Sketch068 [N_Axis]
  Refine = true
  Reversed = true
  SideType = 0
  Suppressed = false
  Type = 0
  Type2 = 0
FEATURE [PartDesign::Body] Body020  label="logo-container-top"
  AllowCompound = false
  Group = -> [Sketch068,Pad030]
  Origin = -> Origin129
  Tip = -> Pad030
PROVENANCE & LICENSES
A FreeCAD (.FCStd) document from a public repository crawl; recipes are the document's own serialized feature recipes (and, for linked parts, companion documents' recipes).
License: mit.
